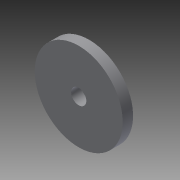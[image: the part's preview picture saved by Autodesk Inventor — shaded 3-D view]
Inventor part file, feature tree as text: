
AUTODESK INVENTOR PART (.ipt)
format: ipt  version: 2015 (Build 190159000, 159)  size: 111,616 bytes
history: native  units: mm
features: extrude x5, sketch x5
ambient origin geometry x8: Origin, YZ Plane, XZ Plane, XY Plane, X Axis, Y Axis, Z Axis, Center Point
bodies: Solid1 (feature_tree)
feature tree (10):
  extrude  "Extrusion1"  Depth=6.0mm
  extrude  "Extrusion2"  Depth=4.1mm
  extrude  "Extrusion3"  Depth=1.0mm TaperAngle=0.0deg
  extrude  "Extrusion4"  Depth=3.8mm TaperAngle=0.0deg
  extrude  "Extrusion5"  Depth=3.8mm TaperAngle=0.0deg
  sketch  "Sketch1"  dims[d0=34.65mm d1=6.0mm]
  sketch  "Sketch2"  dims[d2=4.1mm d3=0.0mm d4=29.0mm]
  sketch  "Sketch3"  dims[d5=1.0mm d6=0.0mm d7=1.0mm d8=0.0mm]
  sketch  "Sketch4"  dims[d9=10.0mm d10=3.8mm d11=0.0mm]
  sketch  "Sketch5"  dims[d12=6.0mm d13=3.8mm d14=0.0mm]
